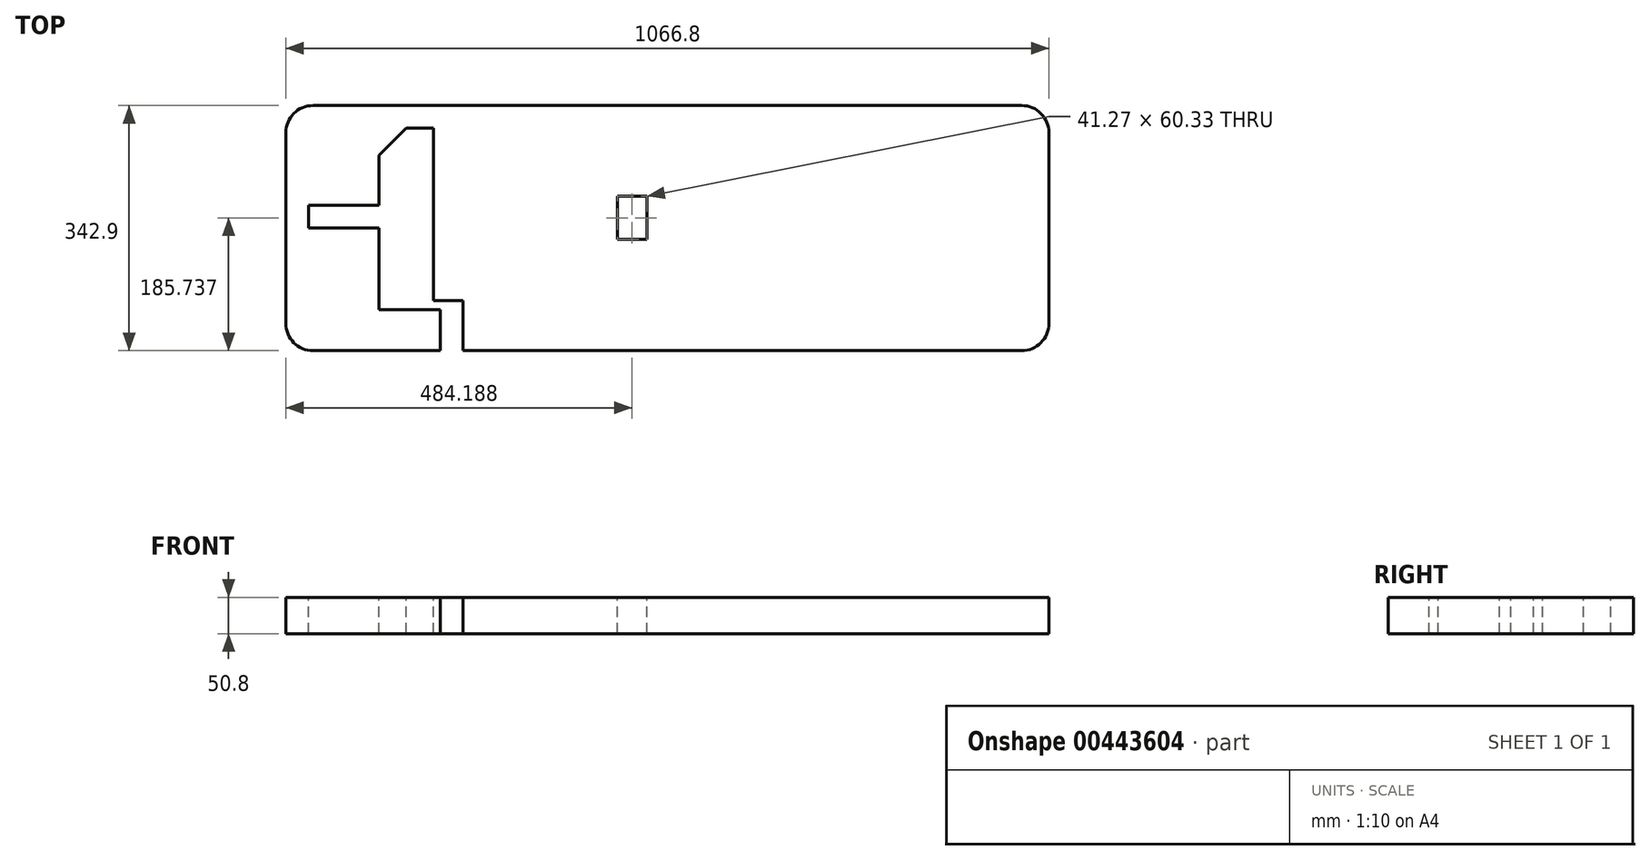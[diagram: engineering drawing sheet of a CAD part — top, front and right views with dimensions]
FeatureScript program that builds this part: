
annotation { "Feature Type Name" : "Feature", "Feature Type Description" : "" }
export const myFeature = defineFeature(function(context is Context, id is Id, definition is map)
    precondition{}
    {
        {
            var Q0;
            Q0=qCreatedBy(makeId("Top.planeOp"),FACE);
            var sketch = newSketch(context, id + "F0", { "sketchPlane" : qUnion([Q0])});
            skLineSegment(sketch, "E0.bottom", {"start": v(533.4, -171.45) * mm, "end": v(-533.4, -171.45) * mm});
            skLineSegment(sketch, "E0.top", {"start": v(533.4, 171.45) * mm, "end": v(-533.4, 171.45) * mm});
            skLineSegment(sketch, "E0.left", {"start": v(533.4, -171.45) * mm, "end": v(533.4, 171.45) * mm});
            skLineSegment(sketch, "E0.right", {"start": v(-533.4, -171.45) * mm, "end": v(-533.4, 171.45) * mm});
            skPoint(sketch, "E0.middle", {"position": v(0, 0) * mm});
            skSolve(sketch);
        }
        {
            var Q0;
            Q0=qSketchRegion(id+"F0",true);
            extrude(context, id + "F1", {"entities" : qUnion([Q0]), "depth" : 50.8 * mm});
        }
        {
            var Q0;
            Q0=makeQuery(id+"F1.opExtrude","CAP_FACE",FACE,{"disambiguationData":[OSD([sQuery(id+"F0.wireOp",EDGE,"E0.bottom"),sQuery(id+"F0.wireOp",EDGE,"E0.top"),sQuery(id+"F0.wireOp",EDGE,"E0.left"),sQuery(id+"F0.wireOp",EDGE,"E0.right")])],"isStart":false});
            var sketch = newSketch(context, id + "F2", { "sketchPlane" : qUnion([Q0])});
            skLineSegment(sketch, "E1", {"start": v(-317.5, -171.45) * mm, "end": v(-285.75, -171.45) * mm});
            skLineSegment(sketch, "E2", {"start": v(-317.5, -171.45) * mm, "end": v(-317.5, -114.3) * mm});
            skLineSegment(sketch, "E3", {"start": v(-285.75, -171.45) * mm, "end": v(-285.75, -101.6) * mm});
            skLineSegment(sketch, "E4", {"start": v(-327.03, -101.6) * mm, "end": v(-285.75, -101.6) * mm});
            skLineSegment(sketch, "E5", {"start": v(-403.23, 101.54) * mm, "end": v(-403.23, 31.75) * mm});
            skLineSegment(sketch, "E6", {"start": v(-403.23, 31.75) * mm, "end": v(-501.65, 31.75) * mm});
            skLineSegment(sketch, "E7", {"start": v(-501.65, 31.75) * mm, "end": v(-501.65, 0) * mm});
            skLineSegment(sketch, "E8", {"start": v(-501.65, 0) * mm, "end": v(-403.23, 0) * mm});
            skLineSegment(sketch, "E9", {"start": v(-403.23, 0) * mm, "end": v(-403.23, -114.3) * mm});
            skLineSegment(sketch, "E10", {"start": v(-403.22, -114.3) * mm, "end": v(-317.5, -114.3) * mm});
            skLineSegment(sketch, "E11", {"start": v(-327.03, 139.7) * mm, "end": v(-365.13, 139.7) * mm});
            skLineSegment(sketch, "E12", {"start": v(-365.13, 139.7) * mm, "end": v(-403.23, 101.54) * mm});
            skLineSegment(sketch, "E13", {"start": v(-327.03, 139.7) * mm, "end": v(-327.03, -101.6) * mm});
            skLineSegment(sketch, "E14.bottom", {"start": v(-28.58, -15.87) * mm, "end": v(-69.85, -15.87) * mm});
            skLineSegment(sketch, "E14.top", {"start": v(-28.58, 44.45) * mm, "end": v(-69.85, 44.45) * mm});
            skLineSegment(sketch, "E14.left", {"start": v(-28.58, -15.87) * mm, "end": v(-28.58, 44.45) * mm});
            skLineSegment(sketch, "E14.right", {"start": v(-69.85, -15.87) * mm, "end": v(-69.85, 44.45) * mm});
            skPoint(sketch, "E14.middle", {"position": v(-49.21, 14.29) * mm});
            skSolve(sketch);
        }
        {
            var Q0;
            Q0=qSketchRegion(id+"F2",true);
            extrude(context, id + "F3", {"entities" : qUnion([Q0]), "operationType" : NewBodyOperationType.REMOVE, "oppositeDirection" : true, "depth" : 50.8 * mm});
        }
        {
            var Q0;
            Q0=makeQuery(id+"F1.opExtrude","SWEPT_EDGE",EDGE,{"disambiguationData":[OSD([sQuery(id+"F0.wireOp",EDGE,"E0.top"),sQuery(id+"F0.wireOp",EDGE,"E0.right")])]});
            var Q1;
            Q1=makeQuery(id+"F1.opExtrude","SWEPT_EDGE",EDGE,{"disambiguationData":[OSD([sQuery(id+"F0.wireOp",EDGE,"E0.bottom"),sQuery(id+"F0.wireOp",EDGE,"E0.right")])]});
            var Q2;
            Q2=makeQuery(id+"F1.opExtrude","SWEPT_EDGE",EDGE,{"disambiguationData":[OSD([sQuery(id+"F0.wireOp",EDGE,"E0.top"),sQuery(id+"F0.wireOp",EDGE,"E0.left")])]});
            var Q3;
            Q3=makeQuery(id+"F1.opExtrude","SWEPT_EDGE",EDGE,{"disambiguationData":[OSD([sQuery(id+"F0.wireOp",EDGE,"E0.bottom"),sQuery(id+"F0.wireOp",EDGE,"E0.left")])]});
            fillet(context, id + "F4", {"entities" : qUnion([Q0, Q1, Q2, Q3]), "radius" : 38.1 * mm, "tangentPropagation" : true, "allowEdgeOverflow" : false});
        }
    });
